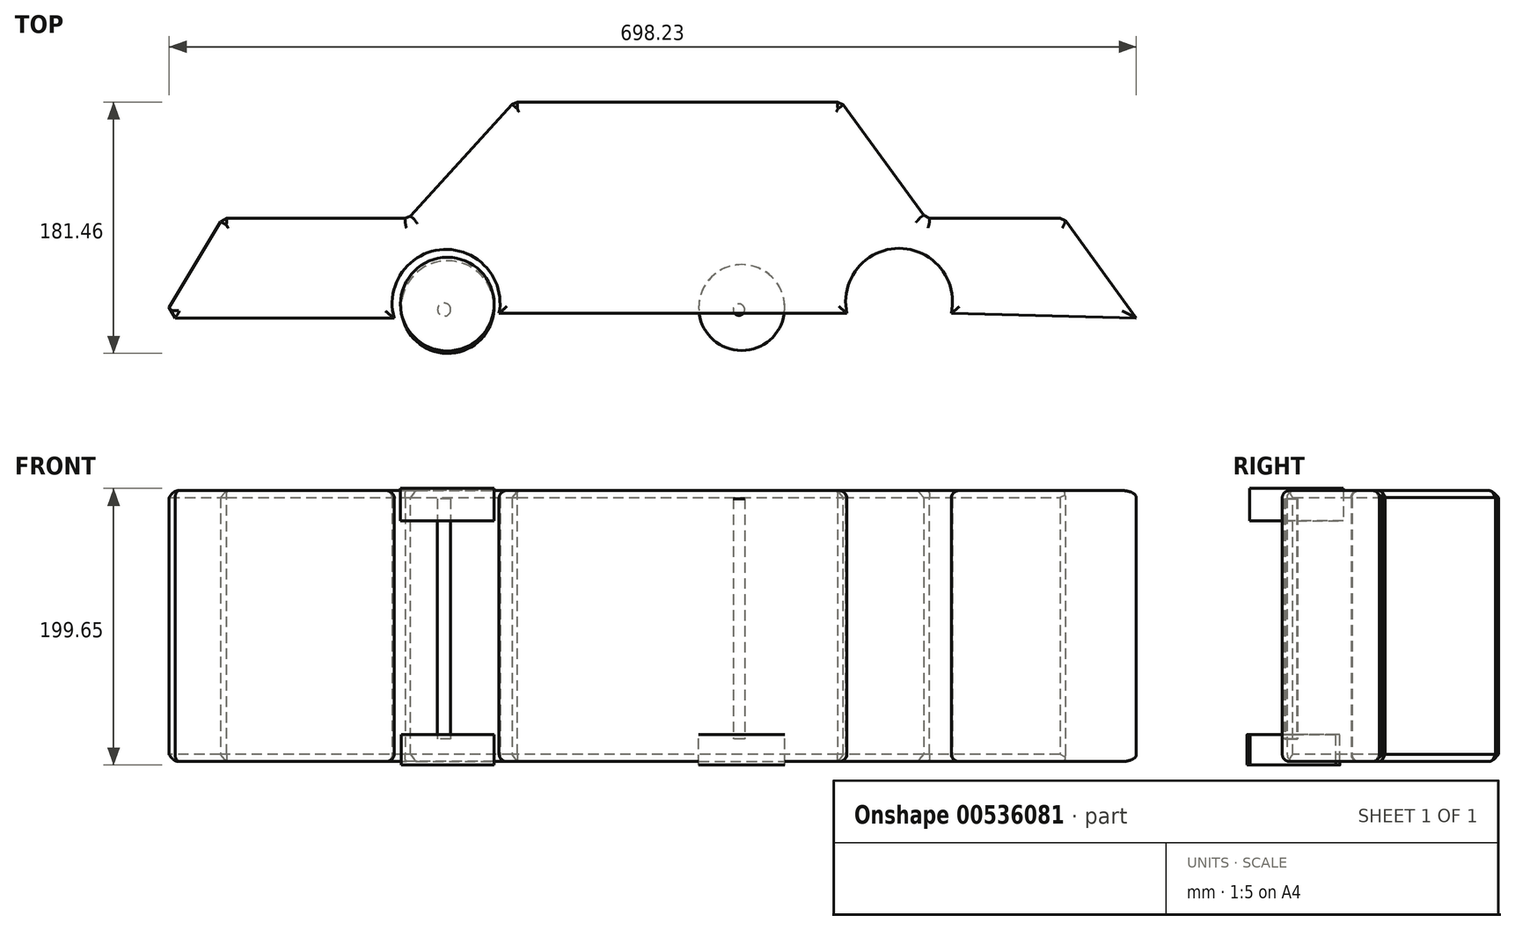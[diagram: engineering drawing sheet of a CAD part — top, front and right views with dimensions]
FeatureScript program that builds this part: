
annotation { "Feature Type Name" : "Feature", "Feature Type Description" : "" }
export const myFeature = defineFeature(function(context is Context, id is Id, definition is map)
    precondition{}
    {
        {
            var Q0;
            Q0=qCreatedBy(makeId("Top.planeOp"),FACE);
            var sketch = newSketch(context, id + "F0", { "sketchPlane" : qUnion([Q0])});
            skLineSegment(sketch, "E0", {"start": v(-154.28, -35.9) * mm, "end": v(154.28, -35.9) * mm});
            skCircle(sketch, "E1", {"center": v(-102.54, -35.9) * mm, "radius": 33.8 * mm});
            skCircle(sketch, "E2", {"center": v(184.85, -35.9) * mm, "radius": 31.06 * mm});
            skSolve(sketch);
        }
        {
            var Q0;
            Q0=qCreatedBy(makeId("Top.planeOp"),FACE);
            var sketch = newSketch(context, id + "F1", { "sketchPlane" : qUnion([Q0])});
            skCircle(sketch, "E3", {"center": v(-102.37, -38.05) * mm, "radius": 33.46 * mm});
            skCircle(sketch, "E4", {"center": v(109.95, -38.41) * mm, "radius": 31.02 * mm});
            skSolve(sketch);
        }
        {
            var Q0;
            Q0 = qSketchRegion(id + "F1", true);
            extrude(context, id + "F2", {"entities" : qUnion([Q0]), "oppositeDirection" : true, "depth" : 176.28 * mm, "offsetDistance" : 25.4 * mm, "hasSecondDirection" : true, "secondDirectionOppositeDirection" : true, "secondDirectionDepth" : 154.18 * mm});
        }
        {
            var Q0;
            {var subQ0=sQuery(id+"F0.wireOp",EDGE,"E1");var subQ1=sQuery(id+"F0.wireOp",EDGE,"E0");var subQ2=makeQuery(id+"F0.imprint","INTERSECT",VERTEX,{"disambiguationData":[OD(0.0)],"derivedFrom":[subQ1,subQ0]});Q0=makeQuery(id+"F0.imprint","IMPRINT",FACE,{"disambiguationData":[TD([[makeQuery(id+"F0.imprint","IMPRINT",EDGE,{"disambiguationData":[TD([[subQ2,-1.0]])],"derivedFrom":subQ1}),-1.0]])]});}
            var Q1;
            {var subQ0=sQuery(id+"F0.wireOp",EDGE,"E1");var subQ1=sQuery(id+"F0.wireOp",EDGE,"E0");var subQ2=makeQuery(id+"F0.imprint","INTERSECT",VERTEX,{"disambiguationData":[OD(0.0)],"derivedFrom":[subQ1,subQ0]});Q1=makeQuery(id+"F0.imprint","IMPRINT",FACE,{"disambiguationData":[TD([[makeQuery(id+"F0.imprint","IMPRINT",EDGE,{"disambiguationData":[TD([[subQ2,-1.0]])],"derivedFrom":subQ1}),1.0]])]});}
            var Q2;
            {var subQ0=sQuery(id+"F0.wireOp",EDGE,"E2");var subQ1=sQuery(id+"F0.wireOp",EDGE,"E0");var subQ2=makeQuery(id+"F0.imprint","INTERSECT",VERTEX,{"disambiguationData":[OD(0.0)],"derivedFrom":[subQ1,subQ0]});Q2=makeQuery(id+"F0.imprint","IMPRINT",FACE,{"disambiguationData":[TD([[makeQuery(id+"F0.imprint","IMPRINT",EDGE,{"disambiguationData":[TD([[subQ2,-1.0]])],"derivedFrom":subQ1}),-1.0]])]});}
            var Q3;
            {var subQ0=sQuery(id+"F0.wireOp",EDGE,"E2");var subQ1=sQuery(id+"F0.wireOp",EDGE,"E0");var subQ2=makeQuery(id+"F0.imprint","INTERSECT",VERTEX,{"disambiguationData":[OD(0.0)],"derivedFrom":[subQ1,subQ0]});Q3=makeQuery(id+"F0.imprint","IMPRINT",FACE,{"disambiguationData":[TD([[makeQuery(id+"F0.imprint","IMPRINT",EDGE,{"disambiguationData":[TD([[subQ2,-1.0]])],"derivedFrom":subQ1}),1.0]])]});}
            extrude(context, id + "F3", {"entities" : qUnion([Q0, Q1, Q2, Q3]), "depth" : 23.37 * mm, "offsetDistance" : 25.4 * mm});
        }
        {
            var Q0;
            Q0=qCreatedBy(makeId("Top.planeOp"),FACE);
            var sketch = newSketch(context, id + "F4", { "sketchPlane" : qUnion([Q0])});
            skCircle(sketch, "E5", {"center": v(-104.87, -39.93) * mm, "radius": 4.74 * mm});
            skCircle(sketch, "E6", {"center": v(107.98, -39.93) * mm, "radius": 4.13 * mm});
            skSolve(sketch);
        }
        {
            var Q0;
            Q0 = qSketchRegion(id + "F4", true);
            extrude(context, id + "F5", {"entities" : qUnion([Q0]), "depth" : 16 * mm, "offsetDistance" : 25.4 * mm, "hasSecondDirection" : true, "secondDirectionOppositeDirection" : true, "secondDirectionDepth" : 157.48 * mm});
        }
        {
            var Q0;
            Q0=qCreatedBy(makeId("Top.planeOp"),FACE);
            var sketch = newSketch(context, id + "F6", { "sketchPlane" : qUnion([Q0])});
            skArc(sketch, "E7", {"start": v(-65.18, -42.56) * mm, "mid": v(-105.28, 3.55) * mm, "end": v(-140.88, -46.12) * mm});
            skArc(sketch, "E8", {"start": v(261.24, -42.56) * mm, "mid": v(223.56, 4.32) * mm, "end": v(185.87, -42.56) * mm});
            skLineSegment(sketch, "E9", {"start": v(-140.88, -46.12) * mm, "end": v(-308, -46.12) * mm});
            skLineSegment(sketch, "E10", {"start": v(-308, -46.12) * mm, "end": v(-264.87, 26.15) * mm});
            skLineSegment(sketch, "E11", {"start": v(-264.87, 26.15) * mm, "end": v(-130.66, 26.15) * mm});
            skLineSegment(sketch, "E12", {"start": v(-130.66, 26.15) * mm, "end": v(-54.15, 109.95) * mm});
            skLineSegment(sketch, "E13", {"start": v(-54.15, 109.95) * mm, "end": v(181.83, 109.95) * mm});
            skLineSegment(sketch, "E14", {"start": v(181.83, 109.95) * mm, "end": v(242.81, 26.15) * mm});
            skLineSegment(sketch, "E15", {"start": v(242.81, 26.15) * mm, "end": v(342.44, 26.15) * mm});
            skLineSegment(sketch, "E16", {"start": v(342.44, 26.15) * mm, "end": v(394.82, -46.12) * mm});
            skLineSegment(sketch, "E17", {"start": v(394.82, -46.12) * mm, "end": v(261.24, -42.56) * mm});
            skLineSegment(sketch, "E18", {"start": v(-65.18, -42.56) * mm, "end": v(185.87, -42.56) * mm});
            skSolve(sketch);
        }
        {
            var Q0;
            Q0 = qSketchRegion(id + "F6", true);
            extrude(context, id + "F7", {"entities" : qUnion([Q0]), "depth" : 21.84 * mm, "offsetDistance" : 25.4 * mm, "hasSecondDirection" : true, "secondDirectionOppositeDirection" : true, "secondDirectionDepth" : 173.74 * mm});
        }
        {
            var Q0;
            Q0=makeQuery(id+"F7.opExtrude","SWEPT_FACE",FACE,{"disambiguationData":[OSD([sQuery(id+"F6.wireOp",EDGE,"E10")])]});
            var Q1;
            Q1=makeQuery(id+"F7.opExtrude","SWEPT_FACE",FACE,{"disambiguationData":[OSD([sQuery(id+"F6.wireOp",EDGE,"E11")])]});
            var Q2;
            Q2=makeQuery(id+"F7.opExtrude","SWEPT_FACE",FACE,{"disambiguationData":[OSD([sQuery(id+"F6.wireOp",EDGE,"E12")])]});
            var Q3;
            Q3=makeQuery(id+"F7.opExtrude","SWEPT_FACE",FACE,{"disambiguationData":[OSD([sQuery(id+"F6.wireOp",EDGE,"E13")])]});
            var Q4;
            Q4=makeQuery(id+"F7.opExtrude","SWEPT_FACE",FACE,{"disambiguationData":[OSD([sQuery(id+"F6.wireOp",EDGE,"E14")])]});
            var Q5;
            Q5=makeQuery(id+"F7.opExtrude","SWEPT_FACE",FACE,{"disambiguationData":[OSD([sQuery(id+"F6.wireOp",EDGE,"E15")])]});
            chamfer(context, id + "F8", {"entities" : qUnion([Q0, Q1, Q2, Q3, Q4, Q5]), "width" : 5.08 * mm, "tangentPropagation" : true});
        }
        {
            var Q0;
            Q0=makeQuery(id+"F7.opExtrude","CAP_FACE",FACE,{"disambiguationData":[OSD([sQuery(id+"F6.wireOp",EDGE,"E7"),sQuery(id+"F6.wireOp",EDGE,"E8"),sQuery(id+"F6.wireOp",EDGE,"E9"),sQuery(id+"F6.wireOp",EDGE,"E10"),sQuery(id+"F6.wireOp",EDGE,"E11"),sQuery(id+"F6.wireOp",EDGE,"E12"),sQuery(id+"F6.wireOp",EDGE,"E13"),sQuery(id+"F6.wireOp",EDGE,"E14"),sQuery(id+"F6.wireOp",EDGE,"E15"),sQuery(id+"F6.wireOp",EDGE,"E16"),sQuery(id+"F6.wireOp",EDGE,"E17"),sQuery(id+"F6.wireOp",EDGE,"E18")])],"isStart":false});
            fillet(context, id + "F9", {"entities" : qUnion([Q0]), "radius" : 5.08 * mm, "tangentPropagation" : true, "allowEdgeOverflow" : false});
        }
        {
            var Q0;
            Q0=makeQuery(id+"F7.opExtrude","CAP_FACE",FACE,{"disambiguationData":[OSD([sQuery(id+"F6.wireOp",EDGE,"E7"),sQuery(id+"F6.wireOp",EDGE,"E8"),sQuery(id+"F6.wireOp",EDGE,"E9"),sQuery(id+"F6.wireOp",EDGE,"E10"),sQuery(id+"F6.wireOp",EDGE,"E11"),sQuery(id+"F6.wireOp",EDGE,"E12"),sQuery(id+"F6.wireOp",EDGE,"E13"),sQuery(id+"F6.wireOp",EDGE,"E14"),sQuery(id+"F6.wireOp",EDGE,"E15"),sQuery(id+"F6.wireOp",EDGE,"E16"),sQuery(id+"F6.wireOp",EDGE,"E17"),sQuery(id+"F6.wireOp",EDGE,"E18")])],"isStart":true});
            fillet(context, id + "F10", {"entities" : qUnion([Q0]), "radius" : 5.08 * mm, "tangentPropagation" : true, "allowEdgeOverflow" : false});
        }
    });
